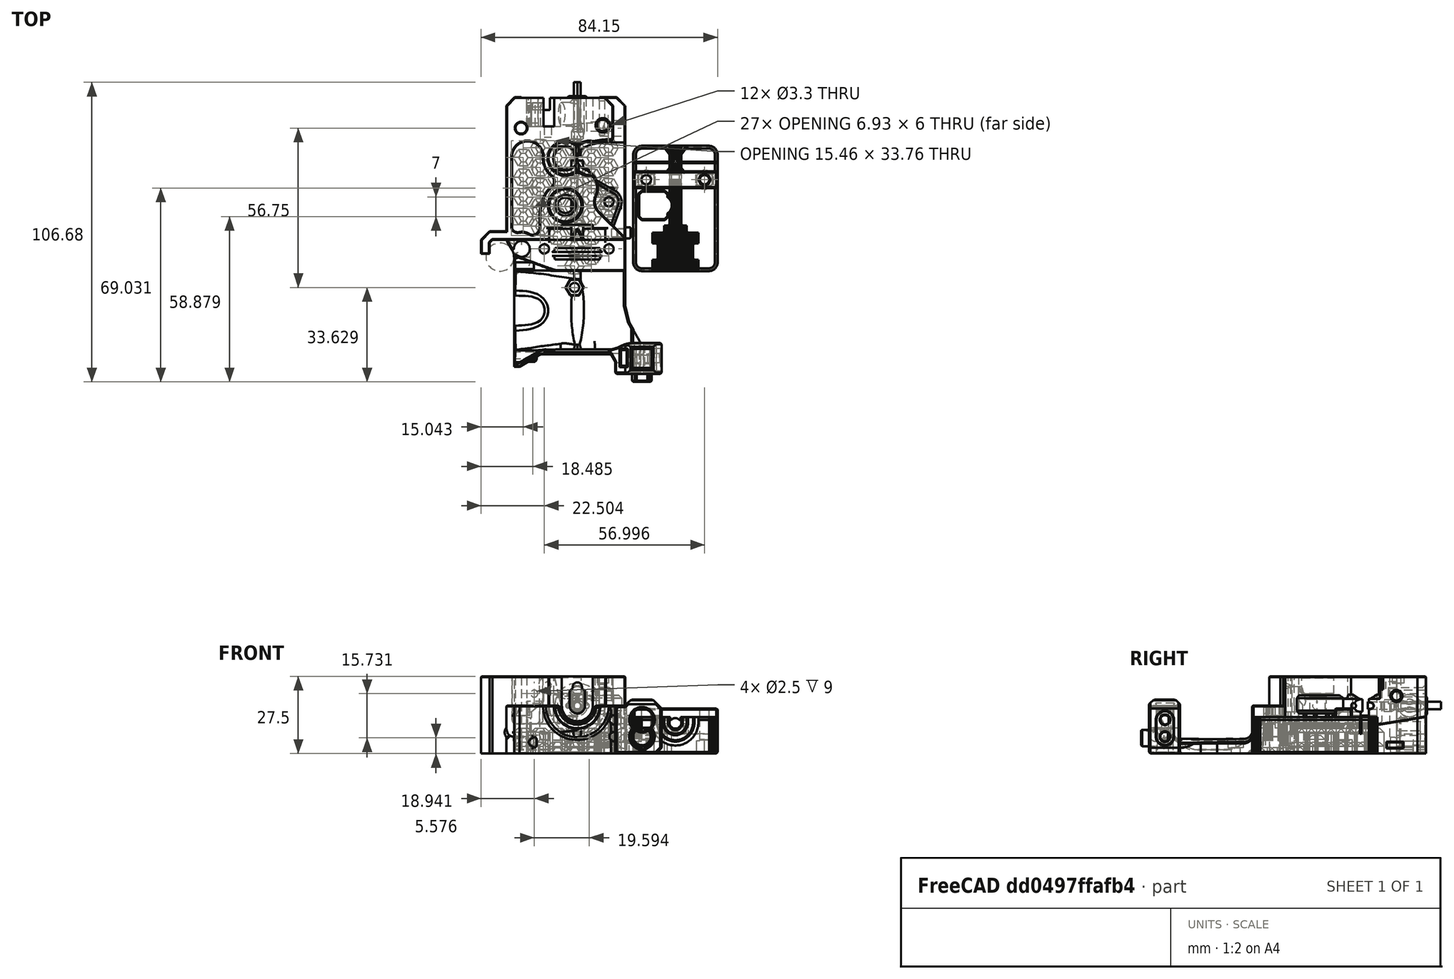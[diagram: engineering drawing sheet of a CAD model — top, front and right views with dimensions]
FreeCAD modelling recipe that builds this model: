
FCSTD DOCUMENT  (FreeCAD 0.18R14555 (Git shallow))
Label: ptfe-bmg
License: All rights reserved
LicenseURL: http://en.wikipedia.org/wiki/All_rights_reserved
objects: Part::Feature×31, Part::Box×27, Part::Cut×25, Part::MultiFuse×15, Part::Cylinder×14, Part::Chamfer×7, Part::MultiCommon×4, App::DocumentObjectGroup×3
note: 123 computed .brp shape members not serialized (recipe doc carries the construction recipe); baked Part::Feature solids carry a one-line shape summary decoded from their .brp

FEATURE [Part::Feature] Part__Feature001  label="ptfe-insert"
  Placement = pos=(4.72,10,0) rot=(0,0,1;0rad)
  shape: bbox 6.822 x 10.5 x 11.73 mm, 34 faces (baked)
FEATURE [Part::Feature] Part__Feature002  label="ptfe-path"
  Placement = pos=(4.72,17,0) rot=(0,0,1;0rad)
  shape: bbox 4.25 x 24 x 4.45 mm, 6 faces (baked)
FEATURE [Part::Feature] Part__Feature003  label="filament-path"
  Placement = pos=(4.72,30,0) rot=(0,0,1;0rad)
  shape: bbox 2.35 x 16 x 2.55 mm, 14 faces (baked)
FEATURE [Part::Feature] PTFE_CUTTER_1_0_1_001001_solid  label="PTFE_CUTTER"
  Placement = pos=(37.03,-6.87,0) rot=(0,0,1;0rad)
  shape: bbox 30 x 35 x 16 mm, 2095 faces (baked)
FEATURE [Part::Box] Box  label="Cube"
  AttacherType = Attacher::AttachEngine3D
  Height = 17
  Length = 33
  Placement = pos=(20,6,0) rot=(0,0,1;0rad)
  Width = 1
FEATURE [Part::Feature] PTFE_CUTTER_1_0_1_001001_solid001  label="PTFE_CUTTER001"
  Placement = pos=(37.03,-6.87,0) rot=(0,0,1;0rad)
  shape: bbox 30 x 35 x 16 mm, 2095 faces (baked)
FEATURE [Part::MultiCommon] Common
  Placement = pos=(0,18.58,0) rot=(0,0,1;0rad)
  Shapes = -> [Box,PTFE_CUTTER_1_0_1_001001_solid001]
FEATURE [Part::Box] Box001  label="Cube001"
  AttacherType = Attacher::AttachEngine3D
  Height = 18
  Length = 32
  Placement = pos=(20,16.32,0) rot=(0,0,1;0rad)
  Width = 6
FEATURE [Part::Box] Box002  label="Cube002"
  AttacherType = Attacher::AttachEngine3D
  Height = 18
  Length = 32
  Placement = pos=(20,16,0) rot=(0,0,1;0rad)
  Width = 15
FEATURE [Part::Feature] PTFE_CUTTER_1_0_1_001001_solid002  label="PTFE_CUTTER002"
  Placement = pos=(37.03,-6.87,0) rot=(0,0,1;0rad)
  shape: bbox 30 x 35 x 16 mm, 2095 faces (baked)
FEATURE [Part::MultiCommon] Common001
  Placement = pos=(0,9.58,0) rot=(0,0,1;0rad)
  Shapes = -> [Box002,PTFE_CUTTER_1_0_1_001001_solid002]
FEATURE [Part::Box] Box003  label="Cube003"
  AttacherType = Attacher::AttachEngine3D
  Height = 18
  Length = 32
  Placement = pos=(20,7,0) rot=(0,0,1;0rad)
  Width = 11
FEATURE [Part::Feature] PTFE_CUTTER_1_0_1_001001_solid003  label="PTFE_CUTTER003"
  Placement = pos=(37.03,-6.87,0) rot=(0,0,1;0rad)
  shape: bbox 30 x 35 x 16 mm, 2095 faces (baked)
FEATURE [Part::MultiCommon] Common002
  Placement = pos=(0,6.58,0) rot=(0,0,1;0rad)
  Shapes = -> [Box003,PTFE_CUTTER_1_0_1_001001_solid003]
FEATURE [Part::Cut] Cut
  Base = -> PTFE_CUTTER_1_0_1_001001_solid
  Tool = -> Box001
FEATURE [Part::MultiFuse] Fusion
  Shapes = -> [Cut,Common002,Common001,Common]
FEATURE [Part::Box] Box004  label="Cube004"
  AttacherType = Attacher::AttachEngine3D
  Height = 10
  Length = 10
  Placement = pos=(23,7,6) rot=(0,0,1;0rad)
  Width = 17.7
FEATURE [Part::Box] Box005  label="Cube005"
  AttacherType = Attacher::AttachEngine3D
  Height = 10
  Length = 10
  Placement = pos=(23,25.5,6) rot=(0,0,1;0rad)
  Width = 3.7
FEATURE [Part::MultiFuse] Fusion001
  Shapes = -> [Box005,Box004,Fusion]
FEATURE [Part::Box] Box006  label="Cube006"
  AttacherType = Attacher::AttachEngine3D
  Height = 5
  Length = 1
  Placement = pos=(49.88,-10,1) rot=(0,0,1;0rad)
  Width = 37.5
FEATURE [Part::MultiFuse] Fusion002
  Shapes = -> [Box006,Fusion001]
FEATURE [Part::Box] Box007  label="Cube007"
  AttacherType = Attacher::AttachEngine3D
  Height = 21
  Length = 32
  Placement = pos=(20,13,0) rot=(0,0,1;0rad)
  Width = 2
FEATURE [Part::Feature] Fusion002001  label="Fusion003"
  shape: bbox 30 x 44.58 x 16 mm, 1730 faces (baked)
FEATURE [Part::MultiCommon] Common003
  Placement = pos=(0,-7,0) rot=(0,0,1;0rad)
  Shapes = -> [Box007,Fusion002001]
FEATURE [Part::MultiFuse] Fusion002002
  Shapes = -> [Common003,Fusion002]
FEATURE [Part::Cylinder] Cylinder005  label="ptfe-cut002"
  Angle = 360
  AttacherType = Attacher::AttachEngine3D
  Height = 22
  Placement = pos=(31.19,9.89,0) rot=(0,0,1;0rad)
  Radius = 3.4
FEATURE [Part::Box] Box010  label="Cube010"
  AttacherType = Attacher::AttachEngine3D
  Height = 10
  Length = 32
  Placement = pos=(20,-15,13) rot=(0,0,1;0rad)
  Width = 47
FEATURE [Part::Box] Box011  label="Cube011"
  AttacherType = Attacher::AttachEngine3D
  Height = 24
  Length = 10
  Placement = pos=(23,5,0) rot=(0,0,1;0rad)
  Width = 9.77
FEATURE [Part::Chamfer] Chamfer
  Base = -> Box011
  Edges = 4 edges r=1: [Edge1,Edge3,Edge5,Edge7]
FEATURE [Part::Cylinder] Cylinder006  label="Cylinder"
  Angle = 360
  AttacherType = Attacher::AttachEngine3D
  Height = 30
  Placement = pos=(25.52,19,0) rot=(0,0,1;0rad)
  Radius = 1.65
FEATURE [Part::Cylinder] Cylinder007  label="Cylinder001"
  Angle = 360
  AttacherType = Attacher::AttachEngine3D
  Height = 30
  Placement = pos=(46.23,19,0) rot=(0,0,1;0rad)
  Radius = 1.65
FEATURE [Part::Box] Box012  label="Cube012"
  AttacherType = Attacher::AttachEngine3D
  Height = 3
  Length = 30
  Placement = pos=(20.88,17,13) rot=(0,0,1;0rad)
  Width = 6
FEATURE [Part::Box] Box013  label="Cube013"
  AttacherType = Attacher::AttachEngine3D
  Height = 4
  Length = 3.8
  Placement = pos=(33.98,16,12) rot=(0,0,1;0rad)
  Width = 8
FEATURE [Part::Cylinder] Cylinder008  label="ptfe-tube-pref002"
  Angle = 360
  AttacherType = Attacher::AttachEngine3D
  Height = 32
  Placement = pos=(35.85,27,10.6) rot=(1,0,0;1.5708rad)
  Radius = 2
FEATURE [Part::Cut] Cut001008
  Base = -> Box013
  Placement = pos=(0,1,0) rot=(0,0,1;0rad)
  Tool = -> Cylinder008
FEATURE [Part::Cylinder] Cylinder009  label="Cylinder002"
  Angle = 360
  AttacherType = Attacher::AttachEngine3D
  Height = 30
  Placement = pos=(25.52,20,0) rot=(0,0,1;0rad)
  Radius = 1.65
FEATURE [Part::Cylinder] Cylinder010  label="Cylinder003"
  Angle = 360
  AttacherType = Attacher::AttachEngine3D
  Height = 30
  Placement = pos=(46.23,20,0) rot=(0,0,1;0rad)
  Radius = 1.65
FEATURE [Part::MultiFuse] Fusion002005
  Shapes = -> [Cylinder009,Cylinder010]
FEATURE [Part::Feature] Cut001012003001  label="Cut001012004"
  Placement = pos=(25.52,19,0) rot=(0,0,1;0rad)
  shape: bbox 5.543 x 6.4 x 5 mm, 28 faces (baked)
FEATURE [Part::Feature] Cut001012003002  label="Cut001012005"
  Placement = pos=(46.23,19,0) rot=(0,0,1;0rad)
  shape: bbox 5.543 x 6.4 x 5 mm, 28 faces (baked)
FEATURE [Part::Feature] Body001005  label="Body001"
  Placement = pos=(35.88,25.2,0) rot=(0,0,1;0rad)
  shape: bbox 6.881 x 4.788 x 40 mm, 8 faces (baked)
FEATURE [Part::Feature] Body001006  label="Body002"
  Placement = pos=(35.88,26.02,0) rot=(0,0,1;3.14159rad)
  shape: bbox 12.97 x 8.755 x 40 mm, 8 faces (baked)
FEATURE [Part::Feature] Body001007  label="Body003"
  Placement = pos=(35.88,25.2,10.5) rot=(0,0,1;0rad)
  shape: bbox 12.18 x 7.934 x 34 mm, 5 faces (baked)
FEATURE [Part::MultiFuse] Fusion002008
  Placement = pos=(0,0,7) rot=(0,0,1;0rad)
  Shapes = -> [Body001005,Body001006]
FEATURE [Part::Cut] Cut001012003003
  Base = -> Fusion002002
  Tool = -> Fusion002008
FEATURE [Part::Cut] Cut001012003004
  Base = -> Cut001012003003
  Tool = -> Body001007
FEATURE [Part::Cut] Cut001012003005
  Base = -> Cut001012003004
  Tool = -> Cylinder005
FEATURE [Part::Cut] Cut001012003006
  Base = -> Cut001012003005
  Tool = -> Chamfer
FEATURE [Part::Feature] Part__Feature008  label="filament-path001"
  Placement = pos=(4.72,40,0) rot=(0,0,1;0rad)
  shape: bbox 2.35 x 16 x 2.55 mm, 14 faces (baked)
FEATURE [Part::Cut] Cut001012003011002008002
  Base = -> Cut001012003006
  Tool = -> Cylinder006
FEATURE [Part::Cut] Cut001012003011002008003
  Base = -> Cut001012003011002008002
  Tool = -> Cylinder007
FEATURE [Part::Cut] Cut001012003011002008004
  Base = -> Cut001012003011002008003
  Tool = -> Cut001012003002
FEATURE [Part::Cut] Cut001012003011002008005
  Base = -> Cut001012003011002008004
  Tool = -> Cut001012003001
FEATURE [Part::Cut] Cut001012003011002008006  label="cutter-base"
  Base = -> Cut001012003011002008005
  Tool = -> Box010
FEATURE [Part::Feature] Cut001012003011002008006002  label="cutter-base001"
  shape: bbox 30 x 44.58 x 13 mm, 1519 faces (baked)
FEATURE [Part::Chamfer] Chamfer002002
  Base = -> Cut001012003011002008006002
  Edges = 37 edges r=0.4: [Edge442,Edge443,Edge444,Edge445,Edge446,Edge447,Edge448,Edge449,Edge450,Edge451,Edge452,Edge453,Edge454,Edge455,Edge456,Edge457,Edge458,Edge459,Edge460,Edge461,Edge462,Edge463,Edge464,Edge465,Edge546,Edge549,Edge550,Edge551,Edge552,Edge553,Edge592,Edge593,Edge594,Edge595,Edge596,Edge597,Edge1307]
FEATURE [Part::Chamfer] Chamfer002003  label="cutter-base-rf"
  Base = -> Chamfer002002
  Edges = 8 edges r=1: [Edge389,Edge392,Edge417,Edge421,Edge506,Edge508,Edge530,Edge534]
FEATURE [Part::Box] Box019  label="Cube019"
  AttacherType = Attacher::AttachEngine3D
  Height = 10
  Length = 10
  Placement = pos=(30,23,8) rot=(0,0,1;0rad)
  Width = 10
FEATURE [Part::Cut] Cut001012003011002008006003
  Base = -> Cut001008
  Tool = -> Box019
FEATURE [Part::Cut] Cut001012003011002008006004
  Base = -> Box012
  Tool = -> Fusion002005
FEATURE [Part::MultiFuse] Fusion002009
  Shapes = -> [Cut001012003011002008006004,Cut001012003011002008006003]
FEATURE [Part::Chamfer] Chamfer002004  label="cutter-cap"
  Base = -> Fusion002009
  Edges = 13 edges r=0.4: [Edge1,Edge2,Edge3,Edge7,Edge8,Edge17,Edge18,Edge31,Edge32,Edge33,Edge34,Edge35,Edge41]
  Placement = pos=(0,-1,0) rot=(0,0,1;0rad)
FEATURE [Part::Box] Box026  label="Cube026"
  AttacherType = Attacher::AttachEngine3D
  Height = 21.6
  Length = 5
  Placement = pos=(-17.02,46.38,0) rot=(0,1,0;0.034907rad)
  Width = 10.15
FEATURE [Part::Box] Box027  label="Cube027"
  AttacherType = Attacher::AttachEngine3D
  Height = 18.6
  Length = 5
  Placement = pos=(-17.02,46.38,0) rot=(0,0,1;0rad)
  Width = 10.15
FEATURE [Part::Cut] Cut001012003011002008006006009002  label="filament-sensor-angle"
  Base = -> Box027
  Placement = pos=(0,-8.4,0) rot=(0,0,1;0rad)
  Tool = -> Box026
FEATURE [Part::Box] Box028  label="Cube028"
  AttacherType = Attacher::AttachEngine3D
  Height = 3.35
  Length = 8
  Placement = pos=(8.5,8.5,10.7) rot=(0,0,1;0rad)
  Width = 1
FEATURE [Part::Box] Box029  label="hingle-support-p3"
  AttacherType = Attacher::AttachEngine3D
  Height = 3.35
  Length = 7
  Placement = pos=(8.5,12.8,10.7) rot=(0,0,1;0rad)
  Width = 1
FEATURE [Part::Box] Box030  label="hingle-support-p4"
  AttacherType = Attacher::AttachEngine3D
  Height = 3.35
  Length = 5
  Placement = pos=(9,15.1,10.7) rot=(0,0,1;0rad)
  Width = 1
FEATURE [Part::Box] Box031  label="Cube031"
  AttacherType = Attacher::AttachEngine3D
  Height = 3.35
  Length = 3
  Placement = pos=(11.7,4.8,10.7) rot=(0,0,1;0rad)
  Width = 1
FEATURE [Part::Chamfer] Chamfer002005  label="hingle-support-p2"
  Base = -> Box028
  Edges = 1 edges r=0.5: [Edge1]
FEATURE [Part::Chamfer] Chamfer002006  label="hingle-support-p1"
  Base = -> Box031
  Edges = 1 edges r=0.5: [Edge1]
FEATURE [Part::Cylinder] Cylinder015  label="Cylinder008"
  Angle = 360
  AttacherType = Attacher::AttachEngine3D
  Height = 10
  Placement = pos=(24,-43,6) rot=(1,0,0;1.5708rad)
  Radius = 3.5
FEATURE [Part::Cylinder] Cylinder016  label="Cylinder009"
  Angle = 360
  AttacherType = Attacher::AttachEngine3D
  Height = 10
  Placement = pos=(24,-43,11.5) rot=(1,0,0;1.5708rad)
  Radius = 3.6
FEATURE [Part::Cut] Cut001012003011002008006006009003002
  Base = -> Cylinder015
  Tool = -> Cylinder016
FEATURE [Part::Cylinder] Cylinder017  label="Cylinder010"
  Angle = 360
  AttacherType = Attacher::AttachEngine3D
  Height = 10
  Placement = pos=(19,-48,6) rot=(0,1,0;1.5708rad)
  Radius = 1.65
FEATURE [Part::Cylinder] Cylinder018  label="Cylinder011"
  Angle = 360
  AttacherType = Attacher::AttachEngine3D
  Height = 10
  Placement = pos=(19,-46.6,6) rot=(0,1,0;1.5708rad)
  Radius = 0.5
FEATURE [Part::Cut] Cut001012003011002008006006009003003
  Base = -> Cut001012003011002008006006009003002
  Tool = -> Cylinder017
FEATURE [Part::Cut] Cut001012003011002008006006009003004
  Base = -> Cut001012003011002008006006009003003
  Tool = -> Cylinder018
FEATURE [Part::Chamfer] Chamfer002007  label="brope-spacer"
  Base = -> Cut001012003011002008006006009003004
  Edges = 8 edges r=0.4: [Edge1,Edge2,Edge8,Edge12,Edge13,Edge14,Edge15,Edge16]
FEATURE [Part::Box] Box034  label="probe-support002"
  AttacherType = Attacher::AttachEngine3D
  Height = 0.2
  Length = 9
  Placement = pos=(22,-49,0) rot=(0,0,1;0rad)
  Width = 8
FEATURE [Part::Box] Box035  label="probe-support-mid"
  AttacherType = Attacher::AttachEngine3D
  Height = 0.2
  Length = 9
  Placement = pos=(19.5,-49,8.9) rot=(0,0,1;0rad)
  Width = 8
FEATURE [Part::Cylinder] Cylinder019  label="probe-overhang"
  Angle = 360
  AttacherType = Attacher::AttachEngine3D
  Height = 15
  Placement = pos=(24,-37,15.8) rot=(1,0,0;1.5708rad)
  Radius = 0.6
FEATURE [Part::Box] Box036  label="filament-support-1"
  AttacherType = Attacher::AttachEngine3D
  Height = 2.8
  Length = 2
  Placement = pos=(-14.8,43.98,0) rot=(0,0,1;0rad)
  Width = 2.4
FEATURE [Part::Box] Box037  label="filament-support-002"
  AttacherType = Attacher::AttachEngine3D
  Height = 4.3
  Length = 0.5
  Placement = pos=(-15.92,38.18,8.2) rot=(0,0,1;0rad)
  Width = 8.2
FEATURE [Part::Feature] Part__Feature025004  label="body-back-original004"
  Placement = pos=(-24,-68,-52.6717) rot=(0,0,1;0rad)
  shape: bbox 64.27 x 98.89 x 29.19 mm, 1019 faces (baked)
FEATURE [Part::Feature] Body001010001  label="Body001011"
  shape: bbox 38 x 35.54 x 5 mm, 40 faces (baked)
FEATURE [Part::Cut] Cut001012003011002008006006009003007  label="hex-cut-origin-p1"
  Base = -> Body001010001
  Tool = -> Part__Feature025004
FEATURE [Part::Feature] Body001010002001  label="Body001010003"
  shape: bbox 7.415 x 6.411 x 5 mm, 8 faces (baked)
FEATURE [Part::Feature] Part__Feature025005  label="body-back-original005"
  Placement = pos=(-24,-68,-52.6717) rot=(0,0,1;0rad)
  shape: bbox 64.27 x 98.89 x 29.19 mm, 1019 faces (baked)
FEATURE [Part::Cut] Cut001012003011002008006006009003008  label="hex-cut-origin-p2"
  Base = -> Body001010002001
  Tool = -> Part__Feature025005
FEATURE [App::DocumentObjectGroup] Group  label="Cutter-guide"
  Group = -> [Cut001012003011002008006,Chamfer002003,Chamfer002004]
FEATURE [App::DocumentObjectGroup] Group002  label="Other"
  Group = -> [Chamfer002007]
FEATURE [Part::Feature] Cut001012003011002008006006009003008001  label="hex-cut-origin-p003"
  shape: bbox 6.928 x 6 x 4 mm, 14 faces (baked)
FEATURE [Part::Feature] Cut001012003011002008006006009003007001  label="hex-cut-origin-p004"
  shape: bbox 37.24 x 34 x 4 mm, 336 faces, 24 solids (baked)
FEATURE [Part::Feature] Cut001012003011002008006006009003008002  label="hex-cut-origin-p005"
  Placement = pos=(0,0,2.5) rot=(0,0,1;0rad)
  shape: bbox 6.928 x 6 x 4 mm, 14 faces (baked)
FEATURE [Part::Feature] Cut001012003011002008006006009003008003  label="hex-cut-origin-p006"
  Placement = pos=(0,0,2.5) rot=(0,0,1;0rad)
  shape: bbox 37.24 x 34 x 4 mm, 336 faces, 24 solids (baked)
FEATURE [Part::Feature] Cut001012003011002008006006009003008004  label="hex-cut-origin-p007"
  Placement = pos=(0,0,5) rot=(0,0,1;0rad)
  shape: bbox 37.24 x 34 x 4 mm, 336 faces, 24 solids (baked)
FEATURE [Part::MultiFuse] Fusion002010004002002006  label="full-back-hex-cut"
  Shapes = -> [Cut001012003011002008006006009003008001,Cut001012003011002008006006009003008003,Cut001012003011002008006006009003007001,Cut001012003011002008006006009003008002,Cut001012003011002008006006009003008004]
FEATURE [Part::Feature] Fusion002010004002002006001  label="full-back-hex-cut001"
  shape: bbox 37.24 x 34 x 9 mm, 350 faces, 25 solids (baked)
FEATURE [Part::Feature] Part__Feature  label="Untitled"
  Placement = pos=(-24,-68,-52.6717) rot=(0,0,1;0rad)
  shape: bbox 64.27 x 98.89 x 29.19 mm, 1019 faces (baked)
FEATURE [Part::MultiFuse] Fusion002010004002002006002  label="full-filament-path"
  Shapes = -> [Part__Feature008,Part__Feature003]
FEATURE [Part::MultiFuse] Fusion002010004002002006003  label="full-ptfe-path"
  Shapes = -> [Part__Feature002,Part__Feature001]
FEATURE [Part::Feature] Fusion002010004002002006003001  label="full^ptfe^path001"
  shape: bbox 6.822 x 29.6 x 11.73 mm, 34 faces (baked)
FEATURE [Part::Feature] Fusion002010004002002006002001  label="full-filament-path001"
  shape: bbox 2.35 x 26 x 2.55 mm, 5 faces (baked)
FEATURE [Part::Cut] Cut001012003011002008006006009003008005
  Base = -> Part__Feature
  Tool = -> Fusion002010004002002006001
FEATURE [Part::Cut] Cut001012003011002008006006009003008006
  Base = -> Cut001012003011002008006006009003008005
  Tool = -> Fusion002010004002002006003001
FEATURE [Part::Cut] Cut001012003011002008006006009003008007
  Base = -> Cut001012003011002008006006009003008006
  Tool = -> Fusion002010004002002006002001
FEATURE [Part::Cut] Cut001012003011002008006006009003008008
  Base = -> Cut001012003011002008006006009003008007
  Tool = -> Cylinder019
FEATURE [Part::MultiFuse] Fusion002010004002002006003002002  label="full-custom-support"
  Shapes = -> [Box035,Chamfer002006,Chamfer002005,Box029,Box030,Box034,Box037,Box036]
FEATURE [App::DocumentObjectGroup] Group001  label="Support"
  Group = -> [Fusion002010004002002006003002002]
FEATURE [Part::Feature] Fusion002010004002002006003002002001  label="full-custom-support001"
  shape: bbox 46.92 x 95.38 x 14.05 mm, 50 faces, 8 solids (baked)
FEATURE [Part::Cylinder] Cylinder  label="scew-hole"
  Angle = 360
  AttacherType = Attacher::AttachEngine3D
  Height = 11
  Placement = pos=(12.25,11.13,0) rot=(0,0,1;0rad)
  Radius = 1.6
FEATURE [Part::Cylinder] Cylinder020  label="Cylinder013"
  Angle = 360
  AttacherType = Attacher::AttachEngine3D
  Height = 3.4
  Radius = 3
FEATURE [Part::Box] Box038  label="Cube032"
  AttacherType = Attacher::AttachEngine3D
  Height = 0.2
  Length = 5
  Placement = pos=(1.6,-5,3.2) rot=(0,0,1;0rad)
  Width = 10
FEATURE [Part::Box] Box039  label="Cube033"
  AttacherType = Attacher::AttachEngine3D
  Height = 0.2
  Length = 5
  Placement = pos=(-6.6,-5,3.2) rot=(0,0,1;0rad)
  Width = 10
FEATURE [Part::Box] Box040  label="Cube034"
  AttacherType = Attacher::AttachEngine3D
  Height = 0.4
  Length = 10
  Placement = pos=(-5,-6.6,3) rot=(0,0,1;0rad)
  Width = 5
FEATURE [Part::Box] Box041  label="Cube035"
  AttacherType = Attacher::AttachEngine3D
  Height = 0.4
  Length = 10
  Placement = pos=(-5,1.6,3) rot=(0,0,1;0rad)
  Width = 5
FEATURE [Part::MultiFuse] Fusion002010004002002006003002002002
  Shapes = -> [Box039,Box041,Box038,Box040]
FEATURE [Part::Cut] Cut001012003011002008006006009003008009
  Base = -> Cylinder020
  Placement = pos=(12.25,11.13,0) rot=(0,0,1;0rad)
  Tool = -> Fusion002010004002002006003002002002
FEATURE [Part::Cylinder] Cylinder022  label="screw-base-fill"
  Angle = 360
  AttacherType = Attacher::AttachEngine3D
  Height = 7
  Placement = pos=(12.25,11.13,0) rot=(0,0,1;0rad)
  Radius = 5.3
FEATURE [Part::MultiFuse] Fusion002010004002002006003002002004  label="back-screw"
  Shapes = -> [Cut001012003011002008006006009003008009,Cylinder]
FEATURE [Part::Feature] Fusion002010004002002006003002002004001  label="back-screw001"
  shape: bbox 6 x 6 x 11 mm, 16 faces (baked)
FEATURE [Part::MultiFuse] Fusion002010004002002006003002002004002
  Shapes = -> [Cut001012003011002008006006009003008008,Cylinder022]
FEATURE [Part::Cut] Cut001012003011002008006006009003008010  label="rev1-m1"
  Base = -> Fusion002010004002002006003002002004002
  Tool = -> Fusion002010004002002006003002002004001
FEATURE [Part::Feature] Cut001012003011002008006006009003008010001  label="rev1-m1-rf"
  shape: bbox 64.27 x 98.89 x 29.19 mm, 1020 faces (baked)
FEATURE [Part::MultiFuse] Fusion002010004002002006003002002004003
  Shapes = -> [Cut001012003011002008006006009003008010001,Fusion002010004002002006003002002001]
